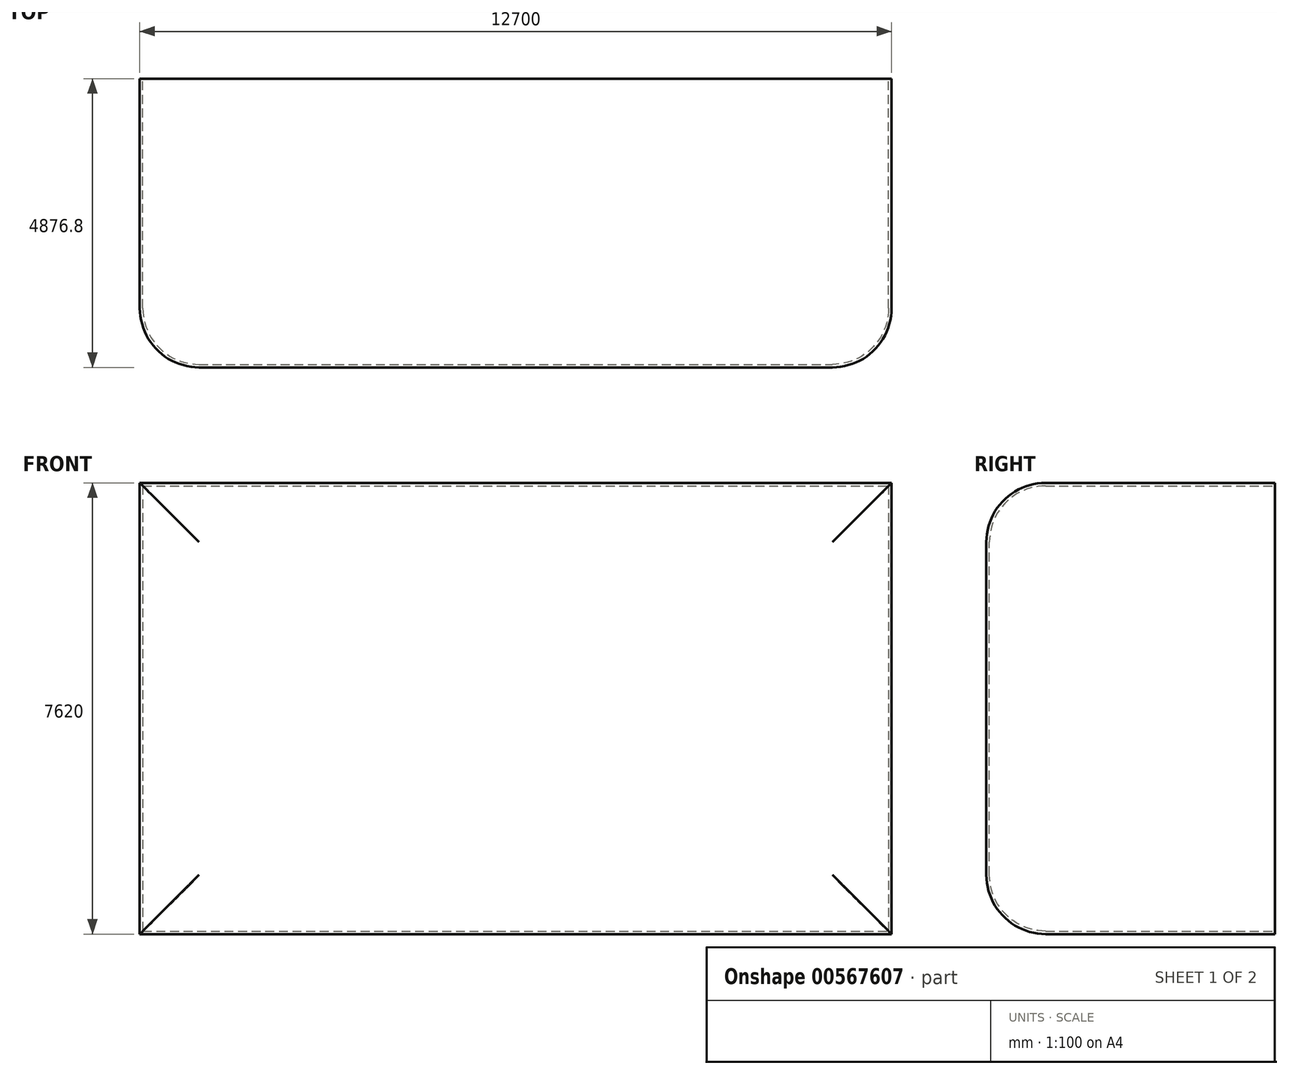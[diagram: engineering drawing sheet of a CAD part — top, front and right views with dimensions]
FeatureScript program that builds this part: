
annotation { "Feature Type Name" : "Feature", "Feature Type Description" : "" }
export const myFeature = defineFeature(function(context is Context, id is Id, definition is map)
    precondition{}
    {
        {
            var Q0;
            Q0=qCreatedBy(makeId("Front.planeOp"),FACE);
            var sketch = newSketch(context, id + "F0", { "sketchPlane" : qUnion([Q0])});
            skLineSegment(sketch, "E0.bottom", {"start": v(-6359.38, 2147.86) * mm, "end": v(6340.62, 2147.86) * mm});
            skLineSegment(sketch, "E0.top", {"start": v(-6359.38, -5472.14) * mm, "end": v(6340.62, -5472.14) * mm});
            skLineSegment(sketch, "E0.left", {"start": v(-6359.38, 2147.86) * mm, "end": v(-6359.38, -5472.14) * mm});
            skLineSegment(sketch, "E0.right", {"start": v(6340.62, 2147.86) * mm, "end": v(6340.62, -5472.14) * mm});
            skSolve(sketch);
        }
        {
            var Q0;
            Q0 = qSketchRegion(id + "F0", true);
            extrude(context, id + "F1", {"entities" : qUnion([Q0]), "depth" : 4876.8 * mm, "offsetDistance" : 25.4 * mm});
        }
        {
            var Q0;
            Q0=makeQuery(id+"F1.opExtrude","CAP_EDGE",EDGE,{"disambiguationData":[OSD([sQuery(id+"F0.wireOp",EDGE,"E0.bottom")])],"isStart":false});
            var Q1;
            Q1=makeQuery(id+"F1.opExtrude","CAP_EDGE",EDGE,{"disambiguationData":[OSD([sQuery(id+"F0.wireOp",EDGE,"E0.left")])],"isStart":false});
            var Q2;
            Q2=makeQuery(id+"F1.opExtrude","CAP_EDGE",EDGE,{"disambiguationData":[OSD([sQuery(id+"F0.wireOp",EDGE,"E0.right")])],"isStart":false});
            var Q3;
            Q3=makeQuery(id+"F1.opExtrude","CAP_EDGE",EDGE,{"disambiguationData":[OSD([sQuery(id+"F0.wireOp",EDGE,"E0.top")])],"isStart":false});
            fillet(context, id + "F2", {"entities" : qUnion([Q0, Q1, Q2, Q3]), "radius" : 1000 * mm, "tangentPropagation" : true, "defaultsChanged" : true, "vertexSettings" : [], "allowEdgeOverflow" : false});
        }
        {
            var Q0;
            Q0=makeQuery(id+"F1.opExtrude","CAP_FACE",FACE,{"disambiguationData":[OSD([sQuery(id+"F0.wireOp",EDGE,"E0.bottom"),sQuery(id+"F0.wireOp",EDGE,"E0.top"),sQuery(id+"F0.wireOp",EDGE,"E0.left"),sQuery(id+"F0.wireOp",EDGE,"E0.right")])],"isStart":true});
            shell(context, id + "F3", {"entities" : qUnion([Q0]), "thickness" : 50.8 * mm});
        }
    });
